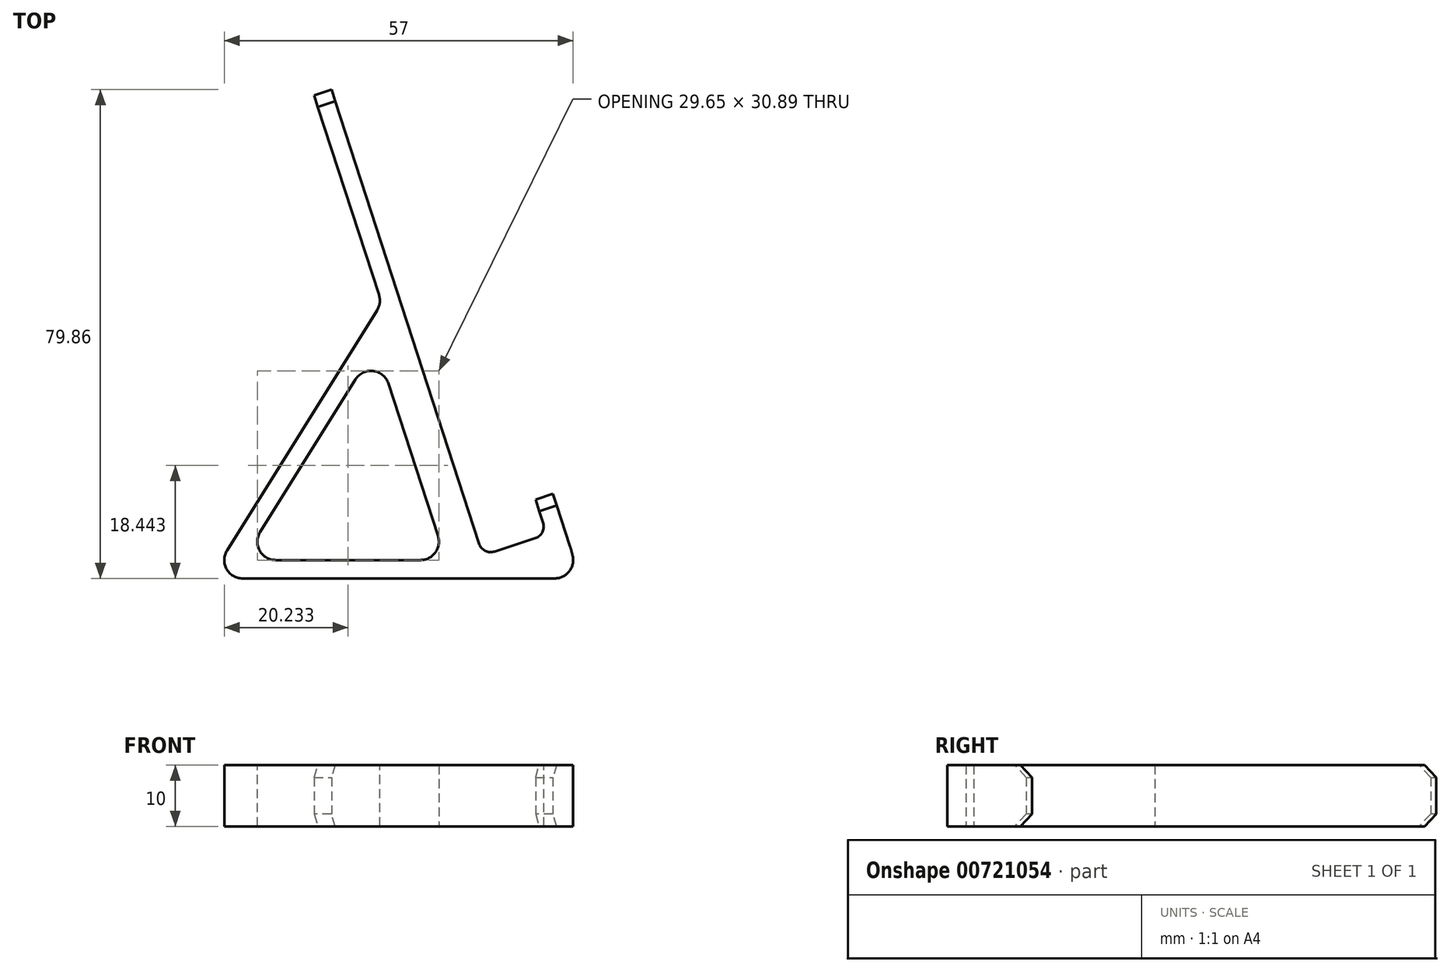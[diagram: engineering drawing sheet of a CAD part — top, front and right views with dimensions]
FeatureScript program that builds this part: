
annotation { "Feature Type Name" : "Feature", "Feature Type Description" : "" }
export const myFeature = defineFeature(function(context is Context, id is Id, definition is map)
    precondition{}
    {
        {
            var Q0;
            Q0=qCreatedBy(makeId("Top.planeOp"),FACE);
            var sketch = newSketch(context, id + "F0", { "sketchPlane" : qUnion([Q0])});
            skLineSegment(sketch, "E0", {"start": v(0, 3.78) * mm, "end": v(10.46, 7.18) * mm});
            skLineSegment(sketch, "E1", {"start": v(10.46, 7.18) * mm, "end": v(8.6, 12.89) * mm});
            skLineSegment(sketch, "E2", {"start": v(0, 3.78) * mm, "end": v(-24.72, 79.86) * mm});
            skLineSegment(sketch, "E3.0", {"start": v(14.24, 5.25) * mm, "end": v(11.46, 13.81) * mm});
            skLineSegment(sketch, "E3.1", {"start": v(-1.93, 0) * mm, "end": v(14.24, 5.25) * mm, "construction": true});
            skLineSegment(sketch, "E3.2", {"start": v(-1.93, 0) * mm, "end": v(-16.55, 45) * mm, "construction": true});
            skLineSegment(sketch, "E4", {"start": v(8.6, 12.89) * mm, "end": v(11.46, 13.81) * mm});
            skLineSegment(sketch, "E5", {"start": v(-27.57, 78.94) * mm, "end": v(-24.72, 79.86) * mm});
            skArc(sketch, "E6", {"start": v(14.24, 5.25) * mm, "mid": v(14.86, 2.66) * mm, "end": v(15.07, 0) * mm});
            skLineSegment(sketch, "E7", {"start": v(15.07, 0) * mm, "end": v(-1.93, 0) * mm});
            skLineSegment(sketch, "E8", {"start": v(-44.67, 0) * mm, "end": v(-16.55, 45) * mm});
            skLineSegment(sketch, "E9", {"start": v(-16.55, 45) * mm, "end": v(-27.57, 78.94) * mm});
            skLineSegment(sketch, "E10", {"start": v(-1.93, 0) * mm, "end": v(-44.67, 0) * mm});
            skLineSegment(sketch, "E11.0", {"start": v(-39.25, 3) * mm, "end": v(-17.41, 37.95) * mm});
            skLineSegment(sketch, "E11.1", {"start": v(-6.06, 3) * mm, "end": v(-39.25, 3) * mm});
            skLineSegment(sketch, "E11.2", {"start": v(-6.06, 3) * mm, "end": v(-17.41, 37.95) * mm});
            skSolve(sketch);
        }
        {
            var Q0;
            Q0=makeQuery(id+"F0.imprint","IMPRINT",FACE,{"disambiguationData":[TD([[makeQuery(id+"F0.imprint","IMPRINT",EDGE,{"derivedFrom":sQuery(id+"F0.wireOp",EDGE,"E0")}),-1.0]])]});
            extrude(context, id + "F1", {"entities" : qUnion([Q0]), "depth" : 10 * mm, "offsetDistance" : 25 * mm, "symmetric" : true});
        }
        {
            var Q0;
            Q0=makeQuery(id+"F1.opExtrude","CAP_EDGE",EDGE,{"disambiguationData":[OSD([sQuery(id+"F0.wireOp",EDGE,"E4")])],"isStart":false});
            var Q1;
            Q1=makeQuery(id+"F1.opExtrude","CAP_EDGE",EDGE,{"disambiguationData":[OSD([sQuery(id+"F0.wireOp",EDGE,"E4")])],"isStart":true});
            var Q2;
            Q2=makeQuery(id+"F1.opExtrude","CAP_EDGE",EDGE,{"disambiguationData":[OSD([sQuery(id+"F0.wireOp",EDGE,"E5")])],"isStart":false});
            var Q3;
            Q3=makeQuery(id+"F1.opExtrude","CAP_EDGE",EDGE,{"disambiguationData":[OSD([sQuery(id+"F0.wireOp",EDGE,"E5")])],"isStart":true});
            chamfer(context, id + "F2", {"entities" : qUnion([Q0, Q1, Q2, Q3]), "width" : 2 * mm, "tangentPropagation" : true});
        }
        {
            var Q0;
            Q0=makeQuery(id+"F1.opExtrude","SWEPT_EDGE",EDGE,{"disambiguationData":[OSD([sQuery(id+"F0.wireOp",EDGE,"E11.0"),sQuery(id+"F0.wireOp",EDGE,"E11.2")])]});
            var Q1;
            Q1=makeQuery(id+"F1.opExtrude","SWEPT_EDGE",EDGE,{"disambiguationData":[OSD([sQuery(id+"F0.wireOp",EDGE,"E11.0"),sQuery(id+"F0.wireOp",EDGE,"E11.1")])]});
            var Q2;
            Q2=makeQuery(id+"F1.opExtrude","SWEPT_EDGE",EDGE,{"disambiguationData":[OSD([sQuery(id+"F0.wireOp",EDGE,"E11.1"),sQuery(id+"F0.wireOp",EDGE,"E11.2")])]});
            var Q3;
            Q3=makeQuery(id+"F1.opExtrude","SWEPT_EDGE",EDGE,{"disambiguationData":[OSD([sQuery(id+"F0.wireOp",EDGE,"E8"),sQuery(id+"F0.wireOp",EDGE,"E10")])]});
            var Q4;
            Q4=makeQuery(id+"F1.opExtrude","SWEPT_EDGE",EDGE,{"disambiguationData":[OSD([sQuery(id+"F0.wireOp",EDGE,"E8"),sQuery(id+"F0.wireOp",EDGE,"E9")])]});
            var Q5;
            Q5=makeQuery(id+"F1.opExtrude","SWEPT_EDGE",EDGE,{"disambiguationData":[OSD([sQuery(id+"F0.wireOp",EDGE,"E6"),sQuery(id+"F0.wireOp",EDGE,"E7")])]});
            fillet(context, id + "F3", {"entities" : qUnion([Q0, Q1, Q2, Q3, Q4, Q5]), "radius" : 3 * mm, "tangentPropagation" : true, "allowEdgeOverflow" : false});
        }
        {
            var Q0;
            Q0=makeQuery(id+"F1.opExtrude","SWEPT_EDGE",EDGE,{"disambiguationData":[OSD([sQuery(id+"F0.wireOp",EDGE,"E0"),sQuery(id+"F0.wireOp",EDGE,"E2")])]});
            var Q1;
            Q1=makeQuery(id+"F1.opExtrude","SWEPT_EDGE",EDGE,{"disambiguationData":[OSD([sQuery(id+"F0.wireOp",EDGE,"E0"),sQuery(id+"F0.wireOp",EDGE,"E1")])]});
            fillet(context, id + "F4", {"entities" : qUnion([Q0, Q1]), "radius" : 2 * mm, "tangentPropagation" : true, "allowEdgeOverflow" : false});
        }
    });
